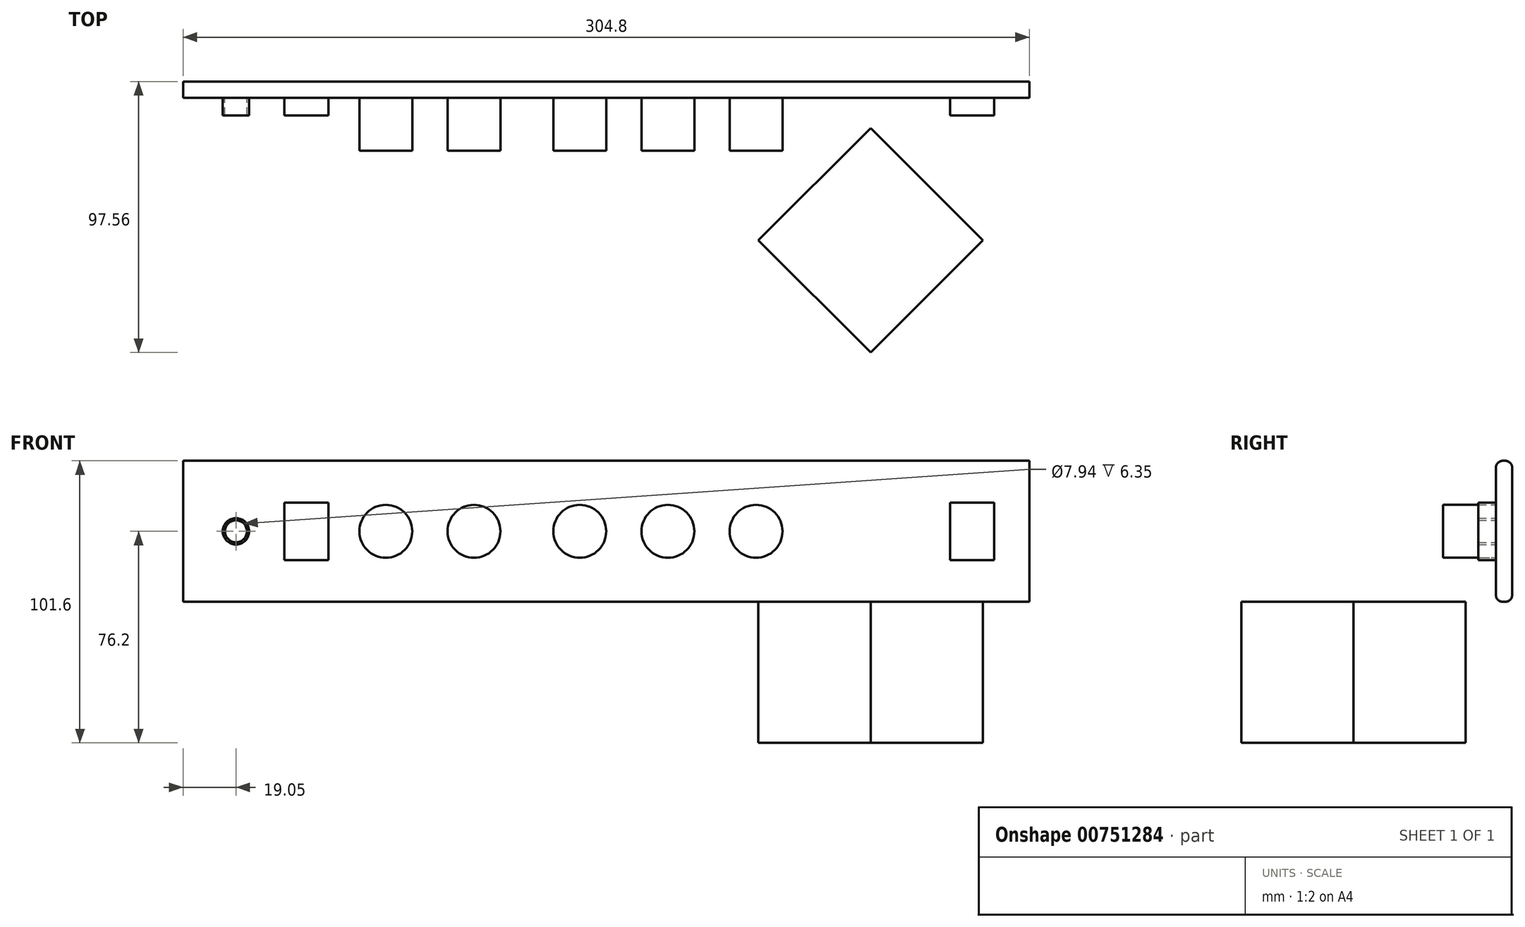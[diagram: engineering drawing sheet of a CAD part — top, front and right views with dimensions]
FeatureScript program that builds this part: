
annotation { "Feature Type Name" : "Feature", "Feature Type Description" : "" }
export const myFeature = defineFeature(function(context is Context, id is Id, definition is map)
    precondition{}
    {
        {
            var Q0;
            Q0=qCreatedBy(makeId("Front.planeOp"),FACE);
            var sketch = newSketch(context, id + "F0", { "sketchPlane" : qUnion([Q0])});
            skLineSegment(sketch, "E0.bottom", {"start": v(152.4, 25.4) * mm, "end": v(-152.4, 25.4) * mm});
            skLineSegment(sketch, "E0.top", {"start": v(152.4, -25.4) * mm, "end": v(-152.4, -25.4) * mm});
            skLineSegment(sketch, "E0.left", {"start": v(152.4, 25.4) * mm, "end": v(152.4, -25.4) * mm});
            skLineSegment(sketch, "E0.right", {"start": v(-152.4, 25.4) * mm, "end": v(-152.4, -25.4) * mm});
            skPoint(sketch, "E0.middle", {"position": v(0, 0) * mm});
            skSolve(sketch);
        }
        {
            var Q0;
            Q0=makeQuery(id+"F0.imprint","IMPRINT",FACE,{"disambiguationData":[TD([[makeQuery(id+"F0.imprint","IMPRINT",EDGE,{"derivedFrom":sQuery(id+"F0.wireOp",EDGE,"E0.bottom")}),1.0]])]});
            extrude(context, id + "F1", {"entities" : qUnion([Q0]), "depth" : (5 + (7 / 8)) * mm, "offsetDistance" : 25.4 * mm});
        }
        {
            var Q0;
            Q0=makeQuery(id+"F1.opExtrude","CAP_FACE",FACE,{"disambiguationData":[OSD([sQuery(id+"F0.wireOp",EDGE,"E0.bottom"),sQuery(id+"F0.wireOp",EDGE,"E0.top"),sQuery(id+"F0.wireOp",EDGE,"E0.left"),sQuery(id+"F0.wireOp",EDGE,"E0.right")])],"isStart":false});
            cPlane(context, id + "F2", {"entities" : qUnion([Q0]), "cplaneType" : CPlaneType.OFFSET, "offset" : 0 * mm, "width" : 152.4 * mm, "height" : 152.4 * mm});
        }
        {
            var Q0;
            Q0=qCreatedBy(id+"F2.planeOp",FACE);
            var sketch = newSketch(context, id + "F3", { "sketchPlane" : qUnion([Q0])});
            skCircle(sketch, "E1", {"center": v(-133.35, 0) * mm, "radius": 4.76 * mm});
            skCircle(sketch, "E2", {"center": v(-133.35, 0) * mm, "radius": 3.97 * mm});
            skLineSegment(sketch, "E3.bottom", {"start": v(-100.01, 10.32) * mm, "end": v(-115.89, 10.32) * mm});
            skLineSegment(sketch, "E3.top", {"start": v(-100.01, -10.32) * mm, "end": v(-115.89, -10.32) * mm});
            skLineSegment(sketch, "E3.left", {"start": v(-100.01, 10.32) * mm, "end": v(-100.01, -10.32) * mm});
            skLineSegment(sketch, "E3.right", {"start": v(-115.89, 10.32) * mm, "end": v(-115.89, -10.32) * mm});
            skPoint(sketch, "E3.middle", {"position": v(-107.95, 0) * mm});
            skLineSegment(sketch, "E4.bottom", {"start": v(139.7, 10.32) * mm, "end": v(123.83, 10.32) * mm});
            skLineSegment(sketch, "E4.top", {"start": v(139.7, -10.32) * mm, "end": v(123.83, -10.32) * mm});
            skLineSegment(sketch, "E4.left", {"start": v(139.7, 10.32) * mm, "end": v(139.7, -10.32) * mm});
            skLineSegment(sketch, "E4.right", {"start": v(123.83, 10.32) * mm, "end": v(123.83, -10.32) * mm});
            skPoint(sketch, "E4.middle", {"position": v(131.76, 0) * mm});
            skSolve(sketch);
        }
        {
            var Q0;
            Q0 = qSketchRegion(id + "F3", true);
            extrude(context, id + "F4", {"entities" : qUnion([Q0]), "operationType" : NewBodyOperationType.ADD, "depth" : 6.35 * mm, "offsetDistance" : 25.4 * mm});
        }
        {
            var Q0;
            Q0=qCreatedBy(id+"F2.planeOp",FACE);
            var sketch = newSketch(context, id + "F5", { "sketchPlane" : qUnion([Q0])});
            skCircle(sketch, "E5", {"center": v(-79.38, 0) * mm, "radius": 9.53 * mm});
            skCircle(sketch, "E6", {"center": v(-47.62, 0) * mm, "radius": 9.53 * mm});
            skCircle(sketch, "E7", {"center": v(-9.52, 0) * mm, "radius": 9.53 * mm});
            skCircle(sketch, "E8", {"center": v(22.23, 0) * mm, "radius": 9.53 * mm});
            skCircle(sketch, "E9", {"center": v(53.98, 0) * mm, "radius": 9.53 * mm});
            skSolve(sketch);
        }
        {
            var Q0;
            Q0=makeQuery(id+"F5.imprint","IMPRINT",FACE,{"disambiguationData":[TD([[makeQuery(id+"F5.imprint","IMPRINT",EDGE,{"derivedFrom":sQuery(id+"F5.wireOp",EDGE,"E5")}),1.0]])]});
            var Q1;
            Q1=makeQuery(id+"F5.imprint","IMPRINT",FACE,{"disambiguationData":[TD([[makeQuery(id+"F5.imprint","IMPRINT",EDGE,{"derivedFrom":sQuery(id+"F5.wireOp",EDGE,"E6")}),1.0]])]});
            var Q2;
            Q2=makeQuery(id+"F5.imprint","IMPRINT",FACE,{"disambiguationData":[TD([[makeQuery(id+"F5.imprint","IMPRINT",EDGE,{"derivedFrom":sQuery(id+"F5.wireOp",EDGE,"E7")}),1.0]])]});
            var Q3;
            Q3=makeQuery(id+"F5.imprint","IMPRINT",FACE,{"disambiguationData":[TD([[makeQuery(id+"F5.imprint","IMPRINT",EDGE,{"derivedFrom":sQuery(id+"F5.wireOp",EDGE,"E8")}),1.0]])]});
            var Q4;
            Q4=makeQuery(id+"F5.imprint","IMPRINT",FACE,{"disambiguationData":[TD([[makeQuery(id+"F5.imprint","IMPRINT",EDGE,{"derivedFrom":sQuery(id+"F5.wireOp",EDGE,"E9")}),1.0]])]});
            extrude(context, id + "F6", {"entities" : qUnion([Q0, Q1, Q2, Q3, Q4]), "operationType" : NewBodyOperationType.ADD, "depth" : 19.05 * mm, "offsetDistance" : 25.4 * mm});
        }
        {
            var Q0;
            Q0=makeQuery(id+"F1.opExtrude","SWEPT_FACE",FACE,{"disambiguationData":[OSD([sQuery(id+"F0.wireOp",EDGE,"E0.top")])]});
            cPlane(context, id + "F7", {"entities" : qUnion([Q0]), "cplaneType" : CPlaneType.OFFSET, "offset" : 0 * mm, "width" : 152.4 * mm, "height" : 152.4 * mm});
        }
        {
            var Q0;
            Q0=qCreatedBy(id+"F7.planeOp",FACE);
            var sketch = newSketch(context, id + "F8", { "sketchPlane" : qUnion([Q0])});
            skLineSegment(sketch, "E10.bottom", {"start": v(95.25, 16.74) * mm, "end": v(54.84, 57.15) * mm});
            skLineSegment(sketch, "E10.top", {"start": v(135.66, 57.15) * mm, "end": v(95.25, 97.56) * mm});
            skLineSegment(sketch, "E10.left", {"start": v(95.25, 16.74) * mm, "end": v(135.66, 57.15) * mm});
            skLineSegment(sketch, "E10.right", {"start": v(54.84, 57.15) * mm, "end": v(95.25, 97.56) * mm});
            skPoint(sketch, "E10.middle", {"position": v(95.25, 57.15) * mm});
            skLineSegment(sketch, "E11", {"start": v(3.18, 0) * mm, "end": v(152.4, 149.23) * mm, "construction": true});
            skSolve(sketch);
        }
        {
            var Q0;
            Q0=makeQuery(id+"F8.imprint","IMPRINT",FACE,{"disambiguationData":[TD([[makeQuery(id+"F8.imprint","IMPRINT",EDGE,{"derivedFrom":sQuery(id+"F8.wireOp",EDGE,"E10.bottom")}),-1.0]])]});
            extrude(context, id + "F9", {"entities" : qUnion([Q0]), "operationType" : NewBodyOperationType.ADD, "depth" : 50.8 * mm, "offsetDistance" : 25.4 * mm});
        }
        {
            var Q0;
            Q0=makeQuery(id+"F1.opExtrude","CAP_EDGE",EDGE,{"disambiguationData":[OSD([sQuery(id+"F0.wireOp",EDGE,"E0.bottom")])],"isStart":false});
            var Q1;
            Q1=makeQuery(id+"F1.opExtrude","CAP_EDGE",EDGE,{"disambiguationData":[OSD([sQuery(id+"F0.wireOp",EDGE,"E0.top")])],"isStart":false});
            var Q2;
            Q2=makeQuery(id+"F1.opExtrude","CAP_EDGE",EDGE,{"disambiguationData":[OSD([sQuery(id+"F0.wireOp",EDGE,"E0.bottom")])],"isStart":true});
            var Q3;
            Q3=makeQuery(id+"F1.opExtrude","CAP_EDGE",EDGE,{"disambiguationData":[OSD([sQuery(id+"F0.wireOp",EDGE,"E0.top")])],"isStart":true});
            fillet(context, id + "F10", {"entities" : qUnion([Q0, Q1, Q2, Q3]), "radius" : 2.54 * mm, "tangentPropagation" : true, "allowEdgeOverflow" : false});
        }
    });
